# Revit family: Turbo_EC
name_source: partatom
category: Mechanical Equipment
units: mm (PartAtom-declared; Revit-internal decimal feet)

## family parameters
Always vertical = Yes
Classification = None
Cut with Voids When Loaded = No
Part Type = Normal
Room Calculation Point = No
Round Connector Dimension = Use Diameter
Shared = No
Work Plane-Based = No

## types (14) — shared parameters
00_20_Manufacturer = Blauberg
Casing Material = Polypropylene
Description = For round channels
Frequency = 50 Hz
Load Classification = HVAC
Maintenance zone material = <By Category>
Manufacturer = Blauberg
Number of Fase = 1
Pressure_Static_Air = 0.0 Pa
URL = https://blaubergventilatoren.de
Voltage = 230 V
zero-valued in all types: Default Elevation

## per-type parameters (varying)
- Turbo 315: 00_20_Name=Inline mixed-flow fan; 00_20_Type=Turbo 315; Amperage=1 A; Apparent Load=327 VA; B=362 mm; D=310 mm; D1=323 mm; D11=325 mm; D2=343 mm; Diameter=310 mm; Dy=306 mm; H=408 mm; Height=408 mm; L=445 mm; L1=355 mm; L2=223 mm; Length=445 mm; Maximum Air Flow=1750.0 m³/h; P=162 mm; Power=315 W; R=155 mm  [stored 0.50853 ft]; R1=162 mm; Ry=153 mm  [stored 0.501969 ft]; Sound pressure level at 3 m distance=52 dBA; Temperature of moving air=+60°С; Weight=11.70 kg; Width=362 mm; d1=318 mm; h=192 mm; r2=172 mm
- Turbo 100: 00_20_Name=Inline mixed-flow fan; 00_20_Type=Turbo 100; Amperage=0 A; Apparent Load=25 VA; B=196 mm; D=97 mm  [stored 0.318241 ft]; D1=164 mm  [stored 0.538058 ft]; D11=166 mm; D2=184 mm; Diameter=97 mm  [stored 0.318241 ft]; Dy=93 mm  [stored 0.305118 ft]; H=241 mm; Height=241 mm; L=303 mm; L1=213 mm; L2=152 mm; Length=303 mm; Maximum Air Flow=220.0 m³/h; P=82 mm  [stored 0.269029 ft]; Power=25 W; R=49 mm  [stored 0.160761 ft]; R1=82 mm  [stored 0.269029 ft]; Ry=47 mm  [stored 0.154199 ft]; Sound pressure level at 3 m distance=32 dBA; Temperature of moving air=+60°С; Weight=1.68 kg; Width=196 mm; d1=159 mm  [stored 0.521654 ft]; h=112 mm  [stored 0.367454 ft]; r2=92 mm  [stored 0.301837 ft]
- Turbo 125: 00_20_Name=Inline mixed-flow fan; 00_20_Type=Turbo 125; Amperage=0 A; Apparent Load=30 VA; B=196 mm; D=123 mm  [stored 0.403543 ft]; D1=164 mm  [stored 0.538058 ft]; D11=166 mm; D2=184 mm; Diameter=123 mm  [stored 0.403543 ft]; Dy=119 mm  [stored 0.39042 ft]; H=241 mm; Height=241 mm; L=258 mm; L1=168 mm; L2=129 mm  [stored 0.423228 ft]; Length=258 mm; Maximum Air Flow=345.0 m³/h; P=82 mm  [stored 0.269029 ft]; Power=29 W; R=62 mm; R1=82 mm  [stored 0.269029 ft]; Ry=60 mm; Sound pressure level at 3 m distance=34 dBA; Temperature of moving air=+60°С; Weight=1.79 kg; Width=196 mm; d1=159 mm  [stored 0.521654 ft]; h=112 mm  [stored 0.367454 ft]; r2=92 mm  [stored 0.301837 ft]
- Turbo 150: 00_20_Name=Inline mixed-flow fan; 00_20_Type=Turbo 150; Amperage=0 A; Apparent Load=51 VA; B=220 mm; D=148 mm  [stored 0.485564 ft]; D1=187 mm; D11=189 mm; D2=207 mm; Diameter=148 mm  [stored 0.485564 ft]; Dy=144 mm  [stored 0.472441 ft]; H=251 mm; Height=251 mm; L=289 mm; L1=199 mm; L2=145 mm; Length=289 mm; Maximum Air Flow=560.0 m³/h; P=94 mm  [stored 0.308399 ft]; Power=50 W; R=74 mm  [stored 0.242782 ft]; R1=94 mm  [stored 0.308399 ft]; Ry=72 mm  [stored 0.23622 ft]; Sound pressure level at 3 m distance=44 dBA; Temperature of moving air=+60°С; Weight=3.18 kg; Width=220 mm; d1=182 mm; h=124 mm; r2=104 mm
- Turbo 160: 00_20_Name=Inline mixed-flow fan; 00_20_Type=Turbo 160; Amperage=0 A; Apparent Load=51 VA; B=220 mm; D=158 mm; D1=187 mm; D11=189 mm; D2=207 mm; Diameter=158 mm; Dy=154 mm  [stored 0.505249 ft]; H=251 mm; Height=251 mm; L=289 mm; L1=199 mm; L2=145 mm; Length=289 mm; Maximum Air Flow=560.0 m³/h; P=94 mm  [stored 0.308399 ft]; Power=50 W; R=79 mm; R1=94 mm  [stored 0.308399 ft]; Ry=77 mm  [stored 0.252625 ft]; Sound pressure level at 3 m distance=44 dBA; Temperature of moving air=+60°С; Weight=3.23 kg; Width=220 mm; d1=182 mm; h=124 mm; r2=104 mm
- Turbo 200: 00_20_Name=Inline mixed-flow fan; 00_20_Type=Turbo 200; Amperage=0 A; Apparent Load=110 VA; B=239 mm; D=199 mm; D1=209 mm; D11=211 mm; D2=229 mm; Diameter=199 mm; Dy=195 mm; H=261 mm; Height=261 mm; L=296 mm; L1=206 mm; L2=148 mm  [stored 0.485564 ft]; Length=296 mm; Maximum Air Flow=1080.0 m³/h; P=105 mm; Power=108 W; R=100 mm  [stored 0.328084 ft]; R1=105 mm; Ry=98 mm  [stored 0.321522 ft]; Sound pressure level at 3 m distance=45 dBA; Temperature of moving air=+60°С; Weight=3.80 kg; Width=239 mm; d1=204 mm; h=135 mm; r2=115 mm
- Turbo 250: 00_20_Name=Inline mixed-flow fan; 00_20_Type=Turbo 250; Amperage=1 A; Apparent Load=182 VA; B=287 mm; D=247 mm; D1=257 mm; D11=259 mm; D2=277 mm; Diameter=247 mm; Dy=243 mm; H=323 mm; Height=323 mm; L=383 mm; L1=293 mm; L2=192 mm; Length=383 mm; Maximum Air Flow=1360.0 m³/h; P=129 mm  [stored 0.423228 ft]; Power=177 W; R=124 mm; R1=129 mm  [stored 0.423228 ft]; Ry=122 mm; Sound pressure level at 3 m distance=51 dBA; Temperature of moving air=+60°С; Weight=7.83 kg; Width=287 mm; d1=252 mm; h=159 mm  [stored 0.521654 ft]; r2=139 mm
- Turbo EC 100: 00_20_Name=Inline mixed-flow fans with EC motor; 00_20_Type=Turbo EC 100; Amperage=0 A; Apparent Load=67 VA; B=192 mm; D=98 mm  [stored 0.321522 ft]; D1=164 mm  [stored 0.538058 ft]; D11=166 mm; D2=184 mm; Diameter=98 mm  [stored 0.321522 ft]; Dy=94 mm  [stored 0.308399 ft]; H=241 mm; Height=241 mm; L=303 mm; L1=213 mm; L2=151 mm; Length=303 mm; Maximum Air Flow=300.0 m³/h; P=82 mm  [stored 0.269029 ft]; Power=30 W; R=49 mm  [stored 0.160761 ft]; R1=82 mm  [stored 0.269029 ft]; Ry=47 mm  [stored 0.154199 ft]; Sound pressure level at 3 m distance=47 dBA; Temperature of moving air=-25…+55 °С; Weight=1.75 kg; Width=192 mm; d1=159 mm  [stored 0.521654 ft]; h=112 mm  [stored 0.367454 ft]; r2=92 mm  [stored 0.301837 ft]
- Turbo EC 125: 00_20_Name=Inline mixed-flow fans with EC motor; 00_20_Type=Turbo EC 125; Amperage=0 A; Apparent Load=85 VA; B=193 mm; D=123 mm  [stored 0.403543 ft]; D1=164 mm  [stored 0.538058 ft]; D11=166 mm; D2=184 mm; Diameter=123 mm  [stored 0.403543 ft]; Dy=119 mm  [stored 0.39042 ft]; H=241 mm; Height=241 mm; L=259 mm; L1=169 mm; L2=129 mm  [stored 0.423228 ft]; Length=259 mm; Maximum Air Flow=450.0 m³/h; P=82 mm  [stored 0.269029 ft]; Power=40 W; R=62 mm; R1=82 mm  [stored 0.269029 ft]; Ry=60 mm; Sound pressure level at 3 m distance=49 dBA; Temperature of moving air=-25…+55 °С; Weight=2.15 kg; Width=193 mm; d1=159 mm  [stored 0.521654 ft]; h=112 mm  [stored 0.367454 ft]; r2=92 mm  [stored 0.301837 ft]
- Turbo EC 150: 00_20_Name=Inline mixed-flow fans with EC motor; 00_20_Type=Turbo EC 150; Amperage=0 A; Apparent Load=110 VA; B=217 mm; D=148 mm  [stored 0.485564 ft]; D1=187 mm; D11=189 mm; D2=207 mm; Diameter=148 mm  [stored 0.485564 ft]; Dy=144 mm  [stored 0.472441 ft]; H=254 mm; Height=254 mm; L=289 mm; L1=199 mm; L2=145 mm; Length=289 mm; Maximum Air Flow=600.0 m³/h; P=94 mm  [stored 0.308399 ft]; Power=55 W; R=74 mm  [stored 0.242782 ft]; R1=94 mm  [stored 0.308399 ft]; Ry=72 mm  [stored 0.23622 ft]; Sound pressure level at 3 m distance=46 dBA; Temperature of moving air=-25…+55 °С; Weight=2.30 kg; Width=217 mm; d1=182 mm; h=124 mm; r2=104 mm
- Turbo EC 160: 00_20_Name=Inline mixed-flow fans with EC motor; 00_20_Type=Turbo EC 160; Amperage=0 A; Apparent Load=110 VA; B=217 mm; D=158 mm; D1=187 mm; D11=189 mm; D2=207 mm; Diameter=158 mm; Dy=154 mm  [stored 0.505249 ft]; H=254 mm; Height=254 mm; L=289 mm; L1=199 mm; L2=145 mm; Length=289 mm; Maximum Air Flow=600.0 m³/h; P=94 mm  [stored 0.308399 ft]; Power=55 W; R=79 mm; R1=94 mm  [stored 0.308399 ft]; Ry=77 mm  [stored 0.252625 ft]; Sound pressure level at 3 m distance=46 dBA; Temperature of moving air=-25…+55 °С; Weight=3.25 kg; Width=217 mm; d1=182 mm; h=124 mm; r2=104 mm
- Turbo EC 200: 00_20_Name=Inline mixed-flow fans with EC motor; 00_20_Type=Turbo EC 200; Amperage=1 A; Apparent Load=235 VA; B=239 mm; D=198 mm; D1=209 mm; D11=211 mm; D2=229 mm; Diameter=198 mm; Dy=194 mm; H=278 mm; Height=278 mm; L=296 mm; L1=206 mm; L2=148 mm  [stored 0.485564 ft]; Length=296 mm; Maximum Air Flow=1040.0 m³/h; P=105 mm; Power=123 W; R=99 mm  [stored 0.324803 ft]; R1=105 mm; Ry=97 mm  [stored 0.318241 ft]; Sound pressure level at 3 m distance=49 dBA; Temperature of moving air=-25…+55 °С; Weight=3.95 kg; Width=239 mm; d1=204 mm; h=135 mm; r2=115 mm
- Turbo EC 250: 00_20_Name=Inline mixed-flow fans with EC motor; 00_20_Type=Turbo EC 200; Amperage=1 A; Apparent Load=317 VA; B=288 mm; D=247 mm; D1=257 mm; D11=259 mm; D2=277 mm; Diameter=247 mm; Dy=243 mm; H=339 mm; Height=339 mm; L=383 mm; L1=293 mm; L2=192 mm; Length=383 mm; Maximum Air Flow=1285.0 m³/h; P=129 mm  [stored 0.423228 ft]; Power=169 W; R=124 mm; R1=129 mm  [stored 0.423228 ft]; Ry=122 mm; Sound pressure level at 3 m distance=53 dBA; Temperature of moving air=-25…+55 °С; Weight=7.80 kg; Width=288 mm; d1=252 mm; h=159 mm  [stored 0.521654 ft]; r2=139 mm
- Turbo EC 315: 00_20_Name=Inline mixed-flow fans with EC motor; 00_20_Type=Turbo EC 315; Amperage=1 A; Apparent Load=288 VA; B=360 mm; D=309 mm; D1=323 mm; D11=325 mm; D2=343 mm; Diameter=309 mm; Dy=305 mm; H=423 mm; Height=423 mm; L=443 mm; L1=353 mm; L2=222 mm; Length=443 mm; Maximum Air Flow=1970.0 m³/h; P=162 mm; Power=284 W; R=154 mm  [stored 0.505249 ft]; R1=162 mm; Ry=152 mm; Sound pressure level at 3 m distance=55 dBA; Temperature of moving air=-25…+55 °С; Weight=11.95 kg; Width=360 mm; d1=318 mm; h=192 mm; r2=172 mm

note: [stored X ft] marks values corroborated as IEEE doubles in the binary element streams (Revit-internal decimal feet)
